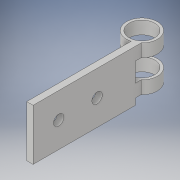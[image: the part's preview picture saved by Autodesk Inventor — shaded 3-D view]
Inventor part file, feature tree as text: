
AUTODESK INVENTOR PART (.ipt)
format: ipt  version: 2018 (Build 220112000, 112)  size: 143,360 bytes
history: native  units: in
note: dims shown in document units (in); Inventor stores cm internally (conversion verified against a paired STEP export)
features: extrude x5, sketch x5, plane x1
ambient origin geometry x8: Origin, YZ Plane, XZ Plane, XY Plane, X Axis, Y Axis, Z Axis, Center Point
bodies: Solid1 (feature_tree)
feature tree (11):
  extrude  "Extrusion1"  Depth=2.0in
  extrude  "Extrusion2"  Depth=0.125in
  plane  "Work Plane1"
  extrude  "Extrusion3"  Depth=0.375in
  extrude  "Extrusion4"  Depth=0.25in
  extrude  "Extrusion5"  Depth=0.75in
  sketch  "Sketch1"  dims[d0=1.0in d1=2.0in]
  sketch  "Sketch2"  dims[d2=0.125in d3=0.0in d4=0.6in]
  sketch  "Sketch3"  dims[d5=0.25in d6=0.0in d7=0.375in]
  sketch  "Sketch4"  dims[d8=0.25in d9=0.0in d10=0.5in]
  sketch  "Sketch5"  dims[d11=5.0in d12=0.0in d13=0.5in d14=0.75in d15=0.2031in d16=0.2031in d17=5.0in d18=0.0in]
